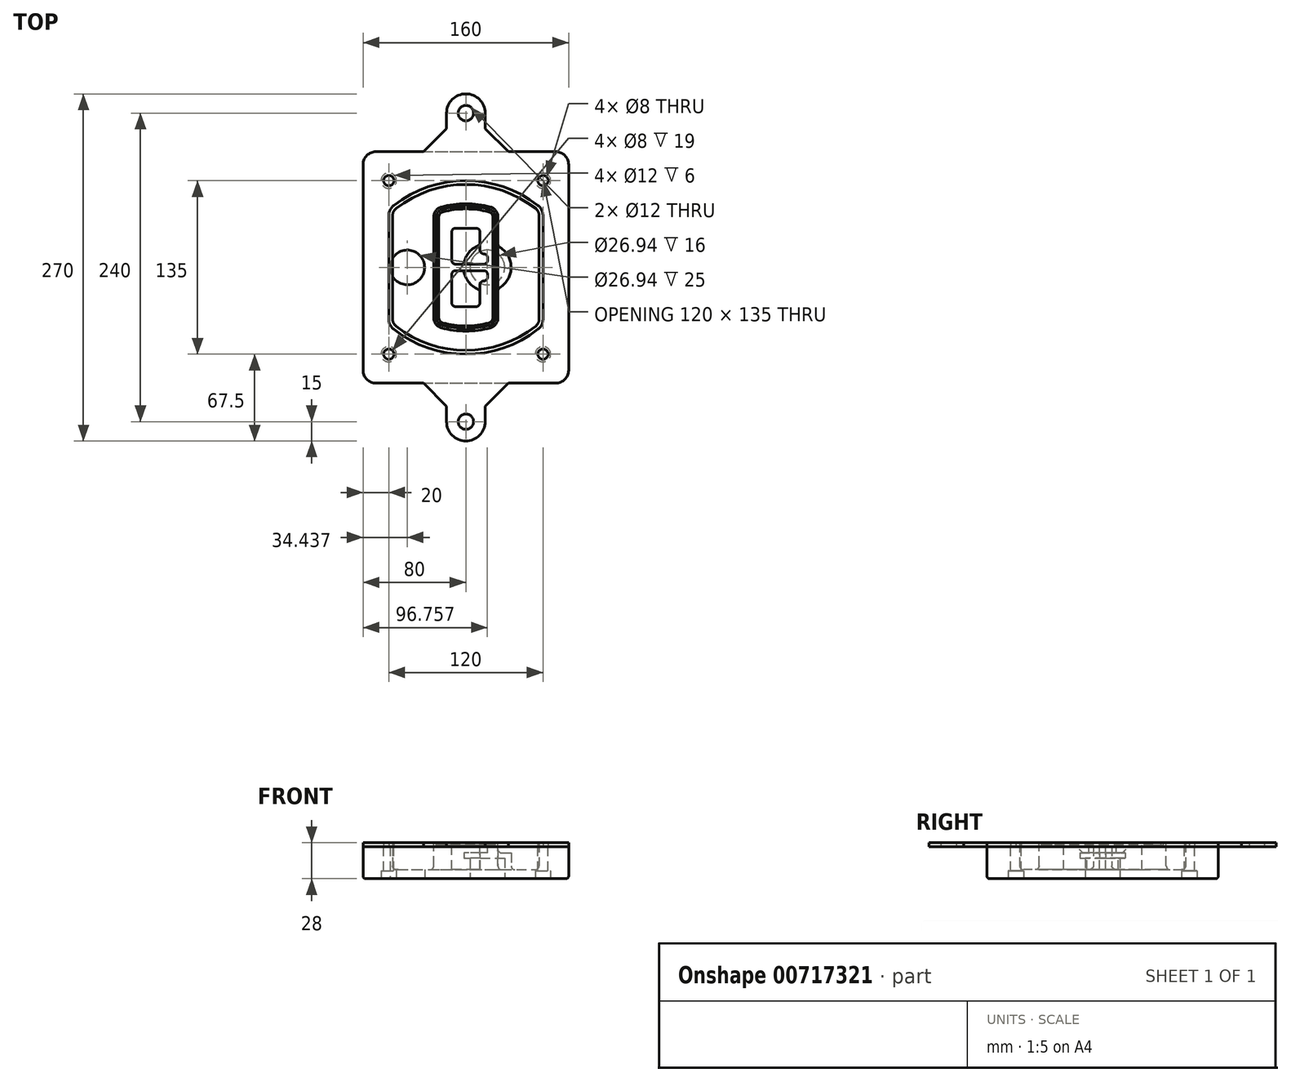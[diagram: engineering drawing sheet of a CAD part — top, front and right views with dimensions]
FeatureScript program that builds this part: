
annotation { "Feature Type Name" : "Feature", "Feature Type Description" : "" }
export const myFeature = defineFeature(function(context is Context, id is Id, definition is map)
    precondition{}
    {
        {
            var Q0;
            Q0=qCreatedBy(makeId("Top.planeOp"),FACE);
            var sketch = newSketch(context, id + "F0", { "sketchPlane" : qUnion([Q0])});
            skPoint(sketch, "E0.rect.middle", {"position": v(0, 0) * mm});
            skLineSegment(sketch, "E1.bottom", {"start": v(-70, -90) * mm, "end": v(70, -90) * mm});
            skLineSegment(sketch, "E1.top", {"start": v(-70, 90) * mm, "end": v(70, 90) * mm});
            skLineSegment(sketch, "E1.left", {"start": v(-80, -80) * mm, "end": v(-80, 80) * mm});
            skLineSegment(sketch, "E1.right", {"start": v(80, -80) * mm, "end": v(80, 80) * mm});
            skLineSegment(sketch, "E2", {"start": v(-80, 90) * mm, "end": v(80, -90) * mm, "construction": true});
            skLineSegment(sketch, "E3", {"start": v(80, 90) * mm, "end": v(-80, -90) * mm, "construction": true});
            skCircle(sketch, "E4", {"center": v(-60, 67.5) * mm, "radius": 4 * mm});
            skCircle(sketch, "E5", {"center": v(60, 67.5) * mm, "radius": 4 * mm});
            skCircle(sketch, "E6", {"center": v(60, -67.5) * mm, "radius": 4 * mm});
            skCircle(sketch, "E7", {"center": v(-60, -67.5) * mm, "radius": 4 * mm});
            skLineSegment(sketch, "E8", {"start": v(-60, 67.5) * mm, "end": v(60, 67.5) * mm, "construction": true});
            skLineSegment(sketch, "E9", {"start": v(60, 67.5) * mm, "end": v(60, -67.5) * mm, "construction": true});
            skLineSegment(sketch, "E10", {"start": v(60, -67.5) * mm, "end": v(-60, -67.5) * mm, "construction": true});
            skLineSegment(sketch, "E11", {"start": v(-60, -67.5) * mm, "end": v(-60, 67.5) * mm, "construction": true});
            skLineSegment(sketch, "E12", {"start": v(-60, 40.3) * mm, "end": v(-60, -40.3) * mm});
            skLineSegment(sketch, "E13", {"start": v(60, 40.3) * mm, "end": v(60, -40.3) * mm});
            skArc(sketch, "E14", {"start": v(56.15, 48.18) * mm, "mid": v(0, 67.5) * mm, "end": v(-56.15, 48.18) * mm});
            skArc(sketch, "E15", {"start": v(-56.15, -48.18) * mm, "mid": v(0, -67.5) * mm, "end": v(56.15, -48.18) * mm});
            skLineSegment(sketch, "E16", {"start": v(-60, 0) * mm, "end": v(60, 0) * mm, "construction": true});
            skPoint(sketch, "E17.visualSharp", {"position": v(-60, -45) * mm});
            skArc(sketch, "E17.filletArc", {"start": v(-60, -40.3) * mm, "mid": v(-58.99, -44.68) * mm, "end": v(-56.15, -48.18) * mm});
            skPoint(sketch, "E18.visualSharp", {"position": v(-60, 45) * mm});
            skArc(sketch, "E18.filletArc", {"start": v(-56.15, 48.18) * mm, "mid": v(-58.99, 44.68) * mm, "end": v(-60, 40.3) * mm});
            skPoint(sketch, "E19.visualSharp", {"position": v(60, 45) * mm});
            skArc(sketch, "E19.filletArc", {"start": v(60, 40.3) * mm, "mid": v(58.99, 44.68) * mm, "end": v(56.15, 48.18) * mm});
            skPoint(sketch, "E20.visualSharp", {"position": v(60, -45) * mm});
            skArc(sketch, "E20.filletArc", {"start": v(56.15, -48.18) * mm, "mid": v(58.99, -44.68) * mm, "end": v(60, -40.3) * mm});
            skPoint(sketch, "E21.visualSharp", {"position": v(-80, 90) * mm});
            skArc(sketch, "E21.filletArc", {"start": v(-70, 90) * mm, "mid": v(-77.07, 87.07) * mm, "end": v(-80, 80) * mm});
            skPoint(sketch, "E22.visualSharp", {"position": v(80, 90) * mm});
            skArc(sketch, "E22.filletArc", {"start": v(80, 80) * mm, "mid": v(77.07, 87.07) * mm, "end": v(70, 90) * mm});
            skPoint(sketch, "E23.visualSharp", {"position": v(80, -90) * mm});
            skArc(sketch, "E23.filletArc", {"start": v(70, -90) * mm, "mid": v(77.07, -87.07) * mm, "end": v(80, -80) * mm});
            skPoint(sketch, "E24.visualSharp", {"position": v(-80, -90) * mm});
            skArc(sketch, "E24.filletArc", {"start": v(-80, -80) * mm, "mid": v(-77.07, -87.07) * mm, "end": v(-70, -90) * mm});
            skArc(sketch, "E25.0", {"start": v(57, 40.3) * mm, "mid": v(56.3, 43.36) * mm, "end": v(54.3, 45.81) * mm});
            skLineSegment(sketch, "E25.1", {"start": v(57, 40.3) * mm, "end": v(57, -40.3) * mm});
            skArc(sketch, "E25.2", {"start": v(54.3, -45.81) * mm, "mid": v(56.3, -43.36) * mm, "end": v(57, -40.3) * mm});
            skArc(sketch, "E25.3", {"start": v(-54.3, -45.81) * mm, "mid": v(0, -64.5) * mm, "end": v(54.3, -45.81) * mm});
            skArc(sketch, "E25.4", {"start": v(-57, -40.3) * mm, "mid": v(-56.3, -43.36) * mm, "end": v(-54.3, -45.81) * mm});
            skArc(sketch, "E25.5", {"start": v(54.3, 45.81) * mm, "mid": v(0, 64.5) * mm, "end": v(-54.3, 45.81) * mm});
            skLineSegment(sketch, "E25.6", {"start": v(-57, 40.3) * mm, "end": v(-57, -40.3) * mm});
            skArc(sketch, "E25.7", {"start": v(-54.3, 45.81) * mm, "mid": v(-56.3, 43.36) * mm, "end": v(-57, 40.3) * mm});
            skArc(sketch, "E26.0", {"start": v(-58.62, 51.33) * mm, "mid": v(-62.58, 46.43) * mm, "end": v(-64, 40.3) * mm});
            skArc(sketch, "E26.1", {"start": v(58.62, 51.33) * mm, "mid": v(0, 71.5) * mm, "end": v(-58.62, 51.33) * mm});
            skArc(sketch, "E26.2", {"start": v(64, 40.3) * mm, "mid": v(62.58, 46.43) * mm, "end": v(58.62, 51.33) * mm});
            skLineSegment(sketch, "E26.3", {"start": v(64, 40.3) * mm, "end": v(64, -40.3) * mm});
            skArc(sketch, "E26.4", {"start": v(58.62, -51.33) * mm, "mid": v(62.58, -46.43) * mm, "end": v(64, -40.3) * mm});
            skLineSegment(sketch, "E26.5", {"start": v(-64, 40.3) * mm, "end": v(-64, -40.3) * mm});
            skArc(sketch, "E26.6", {"start": v(-58.62, -51.33) * mm, "mid": v(0, -71.5) * mm, "end": v(58.62, -51.33) * mm});
            skArc(sketch, "E26.7", {"start": v(-64, -40.3) * mm, "mid": v(-62.58, -46.43) * mm, "end": v(-58.62, -51.33) * mm});
            skSolve(sketch);
        }
        {
            var Q0;
            Q0=makeQuery(id+"F0.imprint","IMPRINT",FACE,{"disambiguationData":[TD([[makeQuery(id+"F0.imprint","IMPRINT",EDGE,{"derivedFrom":sQuery(id+"F0.wireOp",EDGE,"E1.bottom")}),1.0]])]});
            var Q1;
            Q1=makeQuery(id+"F0.imprint","IMPRINT",FACE,{"disambiguationData":[TD([[makeQuery(id+"F0.imprint","IMPRINT",EDGE,{"derivedFrom":sQuery(id+"F0.wireOp",EDGE,"E12")}),1.0]])]});
            var Q2;
            Q2=makeQuery(id+"F0.imprint","IMPRINT",FACE,{"disambiguationData":[TD([[makeQuery(id+"F0.imprint","IMPRINT",EDGE,{"derivedFrom":sQuery(id+"F0.wireOp",EDGE,"E25.0")}),1.0]])]});
            var Q3;
            Q3=makeQuery(id+"F0.imprint","IMPRINT",FACE,{"disambiguationData":[TD([[makeQuery(id+"F0.imprint","IMPRINT",EDGE,{"derivedFrom":sQuery(id+"F0.wireOp",EDGE,"E12")}),-1.0]])]});
            extrude(context, id + "F1", {"entities" : qUnion([Q0, Q1, Q2, Q3]), "oppositeDirection" : true, "depth" : 25 * mm});
        }
        {
            var Q0;
            Q0=makeQuery(id+"F0.imprint","IMPRINT",FACE,{"disambiguationData":[TD([[makeQuery(id+"F0.imprint","IMPRINT",EDGE,{"derivedFrom":sQuery(id+"F0.wireOp",EDGE,"E12")}),1.0]])]});
            extrude(context, id + "F2", {"entities" : qUnion([Q0]), "operationType" : NewBodyOperationType.ADD, "depth" : 3 * mm});
        }
        {
            var Q0;
            Q0=makeQuery(id+"F0.imprint","IMPRINT",FACE,{"disambiguationData":[TD([[makeQuery(id+"F0.imprint","IMPRINT",EDGE,{"derivedFrom":sQuery(id+"F0.wireOp",EDGE,"E25.0")}),1.0]])]});
            extrude(context, id + "F3", {"entities" : qUnion([Q0]), "operationType" : NewBodyOperationType.REMOVE, "oppositeDirection" : true, "depth" : 18 * mm});
        }
        {
            var Q0;
            Q0=makeQuery(id+"F2.opExtrude","CAP_FACE",FACE,{"disambiguationData":[OSD([sQuery(id+"F0.wireOp",EDGE,"E12"),sQuery(id+"F0.wireOp",EDGE,"E13"),sQuery(id+"F0.wireOp",EDGE,"E14"),sQuery(id+"F0.wireOp",EDGE,"E15"),sQuery(id+"F0.wireOp",EDGE,"E17.filletArc"),sQuery(id+"F0.wireOp",EDGE,"E18.filletArc"),sQuery(id+"F0.wireOp",EDGE,"E19.filletArc"),sQuery(id+"F0.wireOp",EDGE,"E20.filletArc"),sQuery(id+"F0.wireOp",EDGE,"E25.0"),sQuery(id+"F0.wireOp",EDGE,"E25.1"),sQuery(id+"F0.wireOp",EDGE,"E25.2"),sQuery(id+"F0.wireOp",EDGE,"E25.3"),sQuery(id+"F0.wireOp",EDGE,"E25.4"),sQuery(id+"F0.wireOp",EDGE,"E25.5"),sQuery(id+"F0.wireOp",EDGE,"E25.6"),sQuery(id+"F0.wireOp",EDGE,"E25.7")])],"isStart":false});
            var sketch = newSketch(context, id + "F4", { "sketchPlane" : qUnion([Q0])});
            skArc(sketch, "E27.0", {"start": v(-19.08, -46.97) * mm, "mid": v(0, -49.5) * mm, "end": v(19.08, -46.97) * mm});
            skArc(sketch, "E28.0", {"start": v(19.08, 46.97) * mm, "mid": v(0, 49.5) * mm, "end": v(-19.08, 46.97) * mm});
            skLineSegment(sketch, "E29", {"start": v(-25, 39.25) * mm, "end": v(-25, -39.25) * mm});
            skLineSegment(sketch, "E30", {"start": v(25, 39.25) * mm, "end": v(25, -39.25) * mm});
            skLineSegment(sketch, "E31", {"start": v(-25, 45.1) * mm, "end": v(25, 45.1) * mm, "construction": true});
            skLineSegment(sketch, "E32", {"start": v(-25, -45.1) * mm, "end": v(25, -45.1) * mm, "construction": true});
            skPoint(sketch, "E33.visualSharp", {"position": v(-25, 45.1) * mm});
            skArc(sketch, "E33.filletArc", {"start": v(-19.08, 46.97) * mm, "mid": v(-23.35, 44.11) * mm, "end": v(-25, 39.25) * mm});
            skPoint(sketch, "E34.visualSharp", {"position": v(25, 45.1) * mm});
            skArc(sketch, "E34.filletArc", {"start": v(25, 39.25) * mm, "mid": v(23.35, 44.11) * mm, "end": v(19.08, 46.97) * mm});
            skPoint(sketch, "E35.visualSharp", {"position": v(25, -45.1) * mm});
            skArc(sketch, "E35.filletArc", {"start": v(19.08, -46.97) * mm, "mid": v(23.35, -44.11) * mm, "end": v(25, -39.25) * mm});
            skPoint(sketch, "E36.visualSharp", {"position": v(-25, -45.1) * mm});
            skArc(sketch, "E36.filletArc", {"start": v(-25, -39.25) * mm, "mid": v(-23.35, -44.11) * mm, "end": v(-19.08, -46.97) * mm});
            skArc(sketch, "E37.0", {"start": v(54.3, 45.81) * mm, "mid": v(0, 64.5) * mm, "end": v(-54.3, 45.81) * mm});
            skArc(sketch, "E37.1", {"start": v(-54.3, 45.81) * mm, "mid": v(-56.3, 43.36) * mm, "end": v(-57, 40.3) * mm});
            skLineSegment(sketch, "E37.2", {"start": v(-57, 40.3) * mm, "end": v(-57, -40.3) * mm});
            skArc(sketch, "E37.3", {"start": v(-57, -40.3) * mm, "mid": v(-56.3, -43.36) * mm, "end": v(-54.3, -45.81) * mm});
            skArc(sketch, "E37.4", {"start": v(-54.3, -45.81) * mm, "mid": v(0, -64.5) * mm, "end": v(54.3, -45.81) * mm});
            skArc(sketch, "E37.5", {"start": v(54.3, -45.81) * mm, "mid": v(56.3, -43.36) * mm, "end": v(57, -40.3) * mm});
            skLineSegment(sketch, "E37.6", {"start": v(57, 40.3) * mm, "end": v(57, -40.3) * mm});
            skArc(sketch, "E37.7", {"start": v(57, 40.3) * mm, "mid": v(56.3, 43.36) * mm, "end": v(54.3, 45.81) * mm});
            skLineSegment(sketch, "E38.0", {"start": v(23, 39.25) * mm, "end": v(23, -39.25) * mm});
            skArc(sketch, "E38.1", {"start": v(18.56, -45.04) * mm, "mid": v(21.76, -42.9) * mm, "end": v(23, -39.25) * mm});
            skArc(sketch, "E38.2", {"start": v(-18.56, -45.04) * mm, "mid": v(0, -47.5) * mm, "end": v(18.56, -45.04) * mm});
            skArc(sketch, "E38.3", {"start": v(-23, -39.25) * mm, "mid": v(-21.76, -42.9) * mm, "end": v(-18.56, -45.04) * mm});
            skLineSegment(sketch, "E38.4", {"start": v(-23, 39.25) * mm, "end": v(-23, -39.25) * mm});
            skArc(sketch, "E38.5", {"start": v(23, 39.25) * mm, "mid": v(21.76, 42.9) * mm, "end": v(18.56, 45.04) * mm});
            skArc(sketch, "E38.6", {"start": v(-18.56, 45.04) * mm, "mid": v(-21.76, 42.9) * mm, "end": v(-23, 39.25) * mm});
            skArc(sketch, "E38.7", {"start": v(18.56, 45.04) * mm, "mid": v(0, 47.5) * mm, "end": v(-18.56, 45.04) * mm});
            skArc(sketch, "E39.0", {"start": v(21, 39.25) * mm, "mid": v(20.18, 41.68) * mm, "end": v(18.04, 43.1) * mm});
            skLineSegment(sketch, "E39.1", {"start": v(21, 39.25) * mm, "end": v(21, -39.25) * mm});
            skArc(sketch, "E39.2", {"start": v(18.04, -43.1) * mm, "mid": v(20.18, -41.68) * mm, "end": v(21, -39.25) * mm});
            skArc(sketch, "E39.3", {"start": v(-18.04, -43.1) * mm, "mid": v(0, -45.5) * mm, "end": v(18.04, -43.1) * mm});
            skArc(sketch, "E39.4", {"start": v(-21, -39.25) * mm, "mid": v(-20.18, -41.68) * mm, "end": v(-18.04, -43.1) * mm});
            skArc(sketch, "E39.5", {"start": v(18.04, 43.1) * mm, "mid": v(0, 45.5) * mm, "end": v(-18.04, 43.1) * mm});
            skLineSegment(sketch, "E39.6", {"start": v(-21, 39.25) * mm, "end": v(-21, -39.25) * mm});
            skArc(sketch, "E39.7", {"start": v(-18.04, 43.1) * mm, "mid": v(-20.18, 41.68) * mm, "end": v(-21, 39.25) * mm});
            skLineSegment(sketch, "E40", {"start": v(-25, 0) * mm, "end": v(25, 0) * mm, "construction": true});
            skLineSegment(sketch, "E41", {"start": v(-11, 5.5) * mm, "end": v(-11, 27.5) * mm});
            skLineSegment(sketch, "E42", {"start": v(-8, 30.5) * mm, "end": v(8, 30.5) * mm});
            skLineSegment(sketch, "E43", {"start": v(11, 27.5) * mm, "end": v(11, 13.5) * mm});
            skLineSegment(sketch, "E44", {"start": v(14, 10.5) * mm, "end": v(14, 10.5) * mm});
            skLineSegment(sketch, "E45", {"start": v(17, 7.5) * mm, "end": v(17, 5.5) * mm});
            skLineSegment(sketch, "E46", {"start": v(14, 2.5) * mm, "end": v(-8, 2.5) * mm});
            skPoint(sketch, "E47.visualSharp", {"position": v(-11, 30.5) * mm});
            skArc(sketch, "E47.filletArc", {"start": v(-8, 30.5) * mm, "mid": v(-10.12, 29.62) * mm, "end": v(-11, 27.5) * mm});
            skPoint(sketch, "E48.visualSharp", {"position": v(11, 30.5) * mm});
            skArc(sketch, "E48.filletArc", {"start": v(11, 27.5) * mm, "mid": v(10.12, 29.62) * mm, "end": v(8, 30.5) * mm});
            skPoint(sketch, "E49.visualSharp", {"position": v(11, 10.5) * mm});
            skArc(sketch, "E49.filletArc", {"start": v(11, 13.5) * mm, "mid": v(11.88, 11.38) * mm, "end": v(14, 10.5) * mm});
            skPoint(sketch, "E50.visualSharp", {"position": v(17, 10.5) * mm});
            skArc(sketch, "E50.filletArc", {"start": v(17, 7.5) * mm, "mid": v(16.12, 9.62) * mm, "end": v(14, 10.5) * mm});
            skPoint(sketch, "E51.visualSharp", {"position": v(17, 2.5) * mm});
            skArc(sketch, "E51.filletArc", {"start": v(14, 2.5) * mm, "mid": v(16.12, 3.38) * mm, "end": v(17, 5.5) * mm});
            skPoint(sketch, "E52.visualSharp", {"position": v(-11, 2.5) * mm});
            skArc(sketch, "E52.filletArc", {"start": v(-11, 5.5) * mm, "mid": v(-10.12, 3.38) * mm, "end": v(-8, 2.5) * mm});
            skLineSegment(sketch, "E53.0.MirrorCS", {"start": v(14, -2.5) * mm, "end": v(-8, -2.5) * mm});
            skArc(sketch, "E54.0.MirrorCS", {"start": v(-11, -5.5) * mm, "mid": v(-10.12, -3.38) * mm, "end": v(-8, -2.5) * mm});
            skLineSegment(sketch, "E55.0.MirrorCS", {"start": v(-11, -5.5) * mm, "end": v(-11, -27.5) * mm});
            skArc(sketch, "E56.0.MirrorCS", {"start": v(-8, -30.5) * mm, "mid": v(-10.12, -29.62) * mm, "end": v(-11, -27.5) * mm});
            skLineSegment(sketch, "E57.0.MirrorCS", {"start": v(-8, -30.5) * mm, "end": v(8, -30.5) * mm});
            skArc(sketch, "E58.0.MirrorCS", {"start": v(11, -27.5) * mm, "mid": v(10.12, -29.62) * mm, "end": v(8, -30.5) * mm});
            skLineSegment(sketch, "E59.0.MirrorCS", {"start": v(11, -27.5) * mm, "end": v(11, -13.5) * mm});
            skArc(sketch, "E60.0.MirrorCS", {"start": v(11, -13.5) * mm, "mid": v(11.88, -11.38) * mm, "end": v(14, -10.5) * mm});
            skArc(sketch, "E61.0.MirrorCS", {"start": v(17, -7.5) * mm, "mid": v(16.12, -9.62) * mm, "end": v(14, -10.5) * mm});
            skLineSegment(sketch, "E62.0.MirrorCS", {"start": v(17, -7.5) * mm, "end": v(17, -5.5) * mm});
            skArc(sketch, "E63.0.MirrorCS", {"start": v(14, -2.5) * mm, "mid": v(16.12, -3.38) * mm, "end": v(17, -5.5) * mm});
            skSolve(sketch);
        }
        {
            var Q0;
            Q0=makeQuery(id+"F4.imprint","IMPRINT",FACE,{"disambiguationData":[TD([[makeQuery(id+"F4.imprint","IMPRINT",EDGE,{"derivedFrom":sQuery(id+"F4.wireOp",EDGE,"E27.0")}),1.0]])]});
            var Q1;
            Q1=makeQuery(id+"F4.imprint","IMPRINT",FACE,{"disambiguationData":[TD([[makeQuery(id+"F4.imprint","IMPRINT",EDGE,{"derivedFrom":sQuery(id+"F4.wireOp",EDGE,"E38.0")}),-1.0]])]});
            var Q2;
            Q2=makeQuery(id+"F4.imprint","IMPRINT",FACE,{"disambiguationData":[TD([[makeQuery(id+"F4.imprint","IMPRINT",EDGE,{"derivedFrom":sQuery(id+"F4.wireOp",EDGE,"E39.0")}),1.0]])]});
            extrude(context, id + "F5", {"entities" : qUnion([Q0, Q1, Q2]), "operationType" : NewBodyOperationType.ADD, "endBound" : BoundingType.UP_TO_NEXT, "oppositeDirection" : true, "depth" : 25 * mm});
        }
        {
            var Q0;
            Q0=makeQuery(id+"F4.imprint","IMPRINT",FACE,{"disambiguationData":[TD([[makeQuery(id+"F4.imprint","IMPRINT",EDGE,{"derivedFrom":sQuery(id+"F4.wireOp",EDGE,"E38.0")}),-1.0]])]});
            extrude(context, id + "F6", {"entities" : qUnion([Q0]), "operationType" : NewBodyOperationType.REMOVE, "oppositeDirection" : true, "depth" : 2 * mm});
        }
        {
            var Q0;
            Q0=makeQuery(id+"F1.opExtrude","CAP_FACE",FACE,{"disambiguationData":[OSD([sQuery(id+"F0.wireOp",EDGE,"E1.bottom"),sQuery(id+"F0.wireOp",EDGE,"E1.top"),sQuery(id+"F0.wireOp",EDGE,"E1.left"),sQuery(id+"F0.wireOp",EDGE,"E1.right"),sQuery(id+"F0.wireOp",EDGE,"E4"),sQuery(id+"F0.wireOp",EDGE,"E5"),sQuery(id+"F0.wireOp",EDGE,"E6"),sQuery(id+"F0.wireOp",EDGE,"E7"),sQuery(id+"F0.wireOp",EDGE,"E21.filletArc"),sQuery(id+"F0.wireOp",EDGE,"E22.filletArc"),sQuery(id+"F0.wireOp",EDGE,"E23.filletArc"),sQuery(id+"F0.wireOp",EDGE,"E24.filletArc")])],"isStart":false});
            var sketch = newSketch(context, id + "F7", { "sketchPlane" : qUnion([Q0])});
            skCircle(sketch, "E64", {"center": v(16.76, 0) * mm, "radius": 13.47 * mm});
            skCircle(sketch, "E65", {"center": v(-45.56, 0) * mm, "radius": 13.47 * mm});
            skLineSegment(sketch, "E66", {"start": v(80, 0) * mm, "end": v(-80, 0) * mm});
            skCircle(sketch, "E67", {"center": v(16.76, 0) * mm, "radius": 18.47 * mm});
            skCircle(sketch, "E68", {"center": v(60, -67.5) * mm, "radius": 6 * mm});
            skCircle(sketch, "E69", {"center": v(-60, -67.5) * mm, "radius": 6 * mm});
            skCircle(sketch, "E70", {"center": v(-60, 67.5) * mm, "radius": 6 * mm});
            skCircle(sketch, "E71", {"center": v(60, 67.5) * mm, "radius": 6 * mm});
            skSolve(sketch);
        }
        {
            var Q0;
            {var subQ1=sQuery(id+"F7.wireOp",EDGE,"E66");var subQ4=sQuery(id+"F7.wireOp",EDGE,"E64");var subQ6=makeQuery(id+"F7.imprint","INTERSECT",VERTEX,{"disambiguationData":[OD(0.0)],"derivedFrom":[subQ4,subQ1]});Q0=makeQuery(id+"F7.imprint","IMPRINT",FACE,{"disambiguationData":[TD([[makeQuery(id+"F7.imprint","IMPRINT",EDGE,{"disambiguationData":[TD([[subQ6,-1.0]])],"derivedFrom":subQ4}),-1.0]])]});}
            var Q1;
            {var subQ0=sQuery(id+"F7.wireOp",EDGE,"E66");var subQ1=sQuery(id+"F7.wireOp",EDGE,"E64");var subQ3=makeQuery(id+"F7.imprint","INTERSECT",VERTEX,{"disambiguationData":[OD(0.0)],"derivedFrom":[subQ1,subQ0]});Q1=makeQuery(id+"F7.imprint","IMPRINT",FACE,{"disambiguationData":[TD([[makeQuery(id+"F7.imprint","IMPRINT",EDGE,{"disambiguationData":[TD([[subQ3,-1.0]])],"derivedFrom":subQ1}),1.0]])]});}
            var Q2;
            {var subQ0=sQuery(id+"F7.wireOp",EDGE,"E66");var subQ1=sQuery(id+"F7.wireOp",EDGE,"E64");var subQ3=makeQuery(id+"F7.imprint","INTERSECT",VERTEX,{"disambiguationData":[OD(0.0)],"derivedFrom":[subQ1,subQ0]});Q2=makeQuery(id+"F7.imprint","IMPRINT",FACE,{"disambiguationData":[TD([[makeQuery(id+"F7.imprint","IMPRINT",EDGE,{"disambiguationData":[TD([[subQ3,1.0]])],"derivedFrom":subQ1}),1.0]])]});}
            var Q3;
            {var subQ1=sQuery(id+"F7.wireOp",EDGE,"E66");var subQ4=sQuery(id+"F7.wireOp",EDGE,"E64");var subQ6=makeQuery(id+"F7.imprint","INTERSECT",VERTEX,{"disambiguationData":[OD(0.0)],"derivedFrom":[subQ4,subQ1]});Q3=makeQuery(id+"F7.imprint","IMPRINT",FACE,{"disambiguationData":[TD([[makeQuery(id+"F7.imprint","IMPRINT",EDGE,{"disambiguationData":[TD([[subQ6,1.0]])],"derivedFrom":subQ4}),-1.0]])]});}
            extrude(context, id + "F8", {"entities" : qUnion([Q0, Q1, Q2, Q3]), "operationType" : NewBodyOperationType.ADD, "oppositeDirection" : true, "depth" : 20 * mm});
        }
        {
            var Q0;
            {var subQ0=sQuery(id+"F7.wireOp",EDGE,"E66");var subQ1=sQuery(id+"F7.wireOp",EDGE,"E64");var subQ3=makeQuery(id+"F7.imprint","INTERSECT",VERTEX,{"disambiguationData":[OD(0.0)],"derivedFrom":[subQ1,subQ0]});Q0=makeQuery(id+"F7.imprint","IMPRINT",FACE,{"disambiguationData":[TD([[makeQuery(id+"F7.imprint","IMPRINT",EDGE,{"disambiguationData":[TD([[subQ3,-1.0]])],"derivedFrom":subQ1}),1.0]])]});}
            var Q1;
            {var subQ0=sQuery(id+"F7.wireOp",EDGE,"E66");var subQ1=sQuery(id+"F7.wireOp",EDGE,"E64");var subQ3=makeQuery(id+"F7.imprint","INTERSECT",VERTEX,{"disambiguationData":[OD(0.0)],"derivedFrom":[subQ1,subQ0]});Q1=makeQuery(id+"F7.imprint","IMPRINT",FACE,{"disambiguationData":[TD([[makeQuery(id+"F7.imprint","IMPRINT",EDGE,{"disambiguationData":[TD([[subQ3,1.0]])],"derivedFrom":subQ1}),1.0]])]});}
            extrude(context, id + "F9", {"entities" : qUnion([Q0, Q1]), "operationType" : NewBodyOperationType.REMOVE, "oppositeDirection" : true, "depth" : 16 * mm});
        }
        {
            var Q0;
            {var subQ0=sQuery(id+"F7.wireOp",EDGE,"E66");var subQ1=sQuery(id+"F7.wireOp",EDGE,"E65");var subQ3=makeQuery(id+"F7.imprint","INTERSECT",VERTEX,{"disambiguationData":[OD(0.0)],"derivedFrom":[subQ1,subQ0]});Q0=makeQuery(id+"F7.imprint","IMPRINT",FACE,{"disambiguationData":[TD([[makeQuery(id+"F7.imprint","IMPRINT",EDGE,{"disambiguationData":[TD([[subQ3,-1.0]])],"derivedFrom":subQ1}),1.0]])]});}
            var Q1;
            {var subQ0=sQuery(id+"F7.wireOp",EDGE,"E66");var subQ1=sQuery(id+"F7.wireOp",EDGE,"E65");var subQ3=makeQuery(id+"F7.imprint","INTERSECT",VERTEX,{"disambiguationData":[OD(0.0)],"derivedFrom":[subQ1,subQ0]});Q1=makeQuery(id+"F7.imprint","IMPRINT",FACE,{"disambiguationData":[TD([[makeQuery(id+"F7.imprint","IMPRINT",EDGE,{"disambiguationData":[TD([[subQ3,1.0]])],"derivedFrom":subQ1}),1.0]])]});}
            extrude(context, id + "F10", {"entities" : qUnion([Q0, Q1]), "operationType" : NewBodyOperationType.REMOVE, "oppositeDirection" : true, "depth" : 25 * mm});
        }
        {
            var Q0;
            Q0=makeQuery(id+"F7.imprint","IMPRINT",FACE,{"disambiguationData":[TD([[makeQuery(id+"F7.imprint","IMPRINT",EDGE,{"derivedFrom":sQuery(id+"F7.wireOp",EDGE,"E68")}),1.0]])]});
            var Q1;
            Q1=makeQuery(id+"F7.imprint","IMPRINT",FACE,{"disambiguationData":[TD([[makeQuery(id+"F7.imprint","IMPRINT",EDGE,{"derivedFrom":makeQuery(id+"F1.opExtrude","CAP_EDGE",EDGE,{"disambiguationData":[OSD([sQuery(id+"F0.wireOp",EDGE,"E5")])],"isStart":false})}),-1.0]])]});
            var Q2;
            Q2=makeQuery(id+"F7.imprint","IMPRINT",FACE,{"disambiguationData":[TD([[makeQuery(id+"F7.imprint","IMPRINT",EDGE,{"derivedFrom":sQuery(id+"F7.wireOp",EDGE,"E69")}),1.0]])]});
            var Q3;
            Q3=makeQuery(id+"F7.imprint","IMPRINT",FACE,{"disambiguationData":[TD([[makeQuery(id+"F7.imprint","IMPRINT",EDGE,{"derivedFrom":makeQuery(id+"F1.opExtrude","CAP_EDGE",EDGE,{"disambiguationData":[OSD([sQuery(id+"F0.wireOp",EDGE,"E4")])],"isStart":false})}),-1.0]])]});
            var Q4;
            Q4=makeQuery(id+"F7.imprint","IMPRINT",FACE,{"disambiguationData":[TD([[makeQuery(id+"F7.imprint","IMPRINT",EDGE,{"derivedFrom":sQuery(id+"F7.wireOp",EDGE,"E70")}),1.0]])]});
            var Q5;
            Q5=makeQuery(id+"F7.imprint","IMPRINT",FACE,{"disambiguationData":[TD([[makeQuery(id+"F7.imprint","IMPRINT",EDGE,{"derivedFrom":makeQuery(id+"F1.opExtrude","CAP_EDGE",EDGE,{"disambiguationData":[OSD([sQuery(id+"F0.wireOp",EDGE,"E7")])],"isStart":false})}),-1.0]])]});
            var Q6;
            Q6=makeQuery(id+"F7.imprint","IMPRINT",FACE,{"disambiguationData":[TD([[makeQuery(id+"F7.imprint","IMPRINT",EDGE,{"derivedFrom":sQuery(id+"F7.wireOp",EDGE,"E71")}),1.0]])]});
            var Q7;
            Q7=makeQuery(id+"F7.imprint","IMPRINT",FACE,{"disambiguationData":[TD([[makeQuery(id+"F7.imprint","IMPRINT",EDGE,{"derivedFrom":makeQuery(id+"F1.opExtrude","CAP_EDGE",EDGE,{"disambiguationData":[OSD([sQuery(id+"F0.wireOp",EDGE,"E6")])],"isStart":false})}),-1.0]])]});
            extrude(context, id + "F11", {"entities" : qUnion([Q0, Q1, Q2, Q3, Q4, Q5, Q6, Q7]), "operationType" : NewBodyOperationType.REMOVE, "oppositeDirection" : true, "depth" : 6 * mm});
        }
        {
            var Q0;
            Q0=makeQuery(id+"F9.boolean.opBoolean","COPY",FACE,{"derivedFrom":makeQuery(id+"F9.opExtrude","CAP_FACE",FACE,{"disambiguationData":[OSD([sQuery(id+"F7.wireOp",EDGE,"E64")])],"isStart":false})});
            var sketch = newSketch(context, id + "F12", { "sketchPlane" : qUnion([Q0])});
            skArc(sketch, "E72.0", {"start": v(11, 17.55) * mm, "mid": v(2.57, 11.82) * mm, "end": v(-1.54, 2.5) * mm});
            skArc(sketch, "E72.1", {"start": v(-1.54, -2.5) * mm, "mid": v(2.57, -11.82) * mm, "end": v(11, -17.55) * mm});
            skLineSegment(sketch, "E73", {"start": v(-1.54, -2.5) * mm, "end": v(14, -2.5) * mm});
            skLineSegment(sketch, "E74.0", {"start": v(14, 2.5) * mm, "end": v(-1.54, 2.5) * mm});
            skArc(sketch, "E74.1", {"start": v(14, 2.5) * mm, "mid": v(16.12, 3.38) * mm, "end": v(17, 5.5) * mm});
            skLineSegment(sketch, "E74.2", {"start": v(17, 7.5) * mm, "end": v(17, 5.5) * mm});
            skArc(sketch, "E74.3", {"start": v(17, 7.5) * mm, "mid": v(16.12, 9.62) * mm, "end": v(14, 10.5) * mm});
            skArc(sketch, "E74.4", {"start": v(11, 13.5) * mm, "mid": v(11.88, 11.38) * mm, "end": v(14, 10.5) * mm});
            skLineSegment(sketch, "E74.5", {"start": v(11, 17.55) * mm, "end": v(11, 13.5) * mm});
            skLineSegment(sketch, "E74.7", {"start": v(14, -2.5) * mm, "end": v(-1.54, -2.5) * mm});
            skArc(sketch, "E74.8", {"start": v(14, -2.5) * mm, "mid": v(16.12, -3.38) * mm, "end": v(17, -5.5) * mm});
            skLineSegment(sketch, "E74.9", {"start": v(17, -7.5) * mm, "end": v(17, -5.5) * mm});
            skArc(sketch, "E74.10", {"start": v(17, -7.5) * mm, "mid": v(16.12, -9.62) * mm, "end": v(14, -10.5) * mm});
            skArc(sketch, "E74.11", {"start": v(11, -13.5) * mm, "mid": v(11.88, -11.38) * mm, "end": v(14, -10.5) * mm});
            skLineSegment(sketch, "E74.12", {"start": v(11, -17.55) * mm, "end": v(11, -13.5) * mm});
            skPoint(sketch, "E75.orphan", {"position": v(11, -27.5) * mm});
            skPoint(sketch, "E76.orphan", {"position": v(-8, -2.5) * mm});
            skPoint(sketch, "E77.orphan", {"position": v(-8, 2.5) * mm});
            skPoint(sketch, "E78.orphan", {"position": v(11, 27.5) * mm});
            skSolve(sketch);
        }
        {
            var Q0;
            {var subQ7=sQuery(id+"F12.wireOp",EDGE,"E72.0");var subQ14=sQuery(id+"F12.wireOp",EDGE,"E72.1");var subQ16=sQuery(id+"F12.wireOp",EDGE,"E74.1");var subQ18=sQuery(id+"F12.wireOp",EDGE,"E74.8");Q0=qUnion([makeQuery(id+"F12.imprint","IMPRINT",FACE,{"disambiguationData":[TD([[makeQuery(id+"F12.imprint","IMPRINT",EDGE,{"derivedFrom":subQ7}),1.0]])]}),makeQuery(id+"F12.imprint","IMPRINT",FACE,{"disambiguationData":[TD([[makeQuery(id+"F12.imprint","IMPRINT",EDGE,{"derivedFrom":subQ14}),1.0]])]}),makeQuery(id+"F12.imprint","IMPRINT",FACE,{"disambiguationData":[TD([[makeQuery(id+"F12.imprint","IMPRINT",EDGE,{"derivedFrom":subQ16}),1.0]])]}),makeQuery(id+"F12.imprint","IMPRINT",FACE,{"disambiguationData":[TD([[makeQuery(id+"F12.imprint","IMPRINT",EDGE,{"derivedFrom":subQ18}),-1.0]])]})]);}
            var Q1;
            Q1=makeQuery(id+"F5.boolean.opBoolean","SPLIT",FACE,{"disambiguationData":[TD([makeQuery(id+"F5.opExtrude","SWEPT_FACE",FACE,{"disambiguationData":[OSD([sQuery(id+"F4.wireOp",EDGE,"E41")])]})])],"derivedFrom":makeQuery(id+"F3.boolean.opBoolean","COPY",FACE,{"derivedFrom":makeQuery(id+"F3.opExtrude","CAP_FACE",FACE,{"disambiguationData":[OSD([sQuery(id+"F0.wireOp",EDGE,"E25.0"),sQuery(id+"F0.wireOp",EDGE,"E25.1"),sQuery(id+"F0.wireOp",EDGE,"E25.2"),sQuery(id+"F0.wireOp",EDGE,"E25.3"),sQuery(id+"F0.wireOp",EDGE,"E25.4"),sQuery(id+"F0.wireOp",EDGE,"E25.5"),sQuery(id+"F0.wireOp",EDGE,"E25.6"),sQuery(id+"F0.wireOp",EDGE,"E25.7")])],"isStart":false})})});
            extrude(context, id + "F13", {"entities" : qUnion([Q0]), "operationType" : NewBodyOperationType.REMOVE, "endBound" : BoundingType.UP_TO_SURFACE, "endBoundEntityFace" : qUnion([Q1]), "depth" : 25 * mm});
        }
        {
            var Q0;
            Q0=makeQuery(id+"F3.boolean.opBoolean","COPY",EDGE,{"derivedFrom":makeQuery(id+"F3.opExtrude","CAP_EDGE",EDGE,{"disambiguationData":[OSD([sQuery(id+"F0.wireOp",EDGE,"E25.6")])],"isStart":false})});
            var Q1;
            Q1=makeQuery(id+"F8.boolean.opBoolean","INTERSECT",EDGE,{"derivedFrom":[makeQuery(id+"F5.opExtrude","SWEPT_FACE",FACE,{"disambiguationData":[OSD([sQuery(id+"F4.wireOp",EDGE,"E30")])]}),makeQuery(id+"F8.opExtrude","CAP_FACE",FACE,{"disambiguationData":[OSD([sQuery(id+"F7.wireOp",EDGE,"E67")])],"isStart":false})]});
            var Q2;
            Q2=makeQuery(id+"F8.boolean.opBoolean","INTERSECT",EDGE,{"disambiguationData":[OD(1.0)],"derivedFrom":[makeQuery(id+"F5.opExtrude","SWEPT_FACE",FACE,{"disambiguationData":[OSD([sQuery(id+"F4.wireOp",EDGE,"E30")])]}),makeQuery(id+"F8.opExtrude","SWEPT_FACE",FACE,{"disambiguationData":[OSD([sQuery(id+"F7.wireOp",EDGE,"E67")])]})]});
            var Q3;
            {var subQ0=sQuery(id+"F4.wireOp",EDGE,"E30");Q3=makeQuery(id+"F8.boolean.opBoolean","SPLIT",EDGE,{"disambiguationData":[TD([makeQuery(id+"F5.opExtrude","SWEPT_FACE",FACE,{"disambiguationData":[OSD([sQuery(id+"F4.wireOp",EDGE,"E35.filletArc")])]})])],"derivedFrom":makeQuery(id+"F5.opExtrude","CAP_EDGE",EDGE,{"disambiguationData":[OSD([subQ0])],"isStart":false})});}
            var Q4;
            {var subQ0=sQuery(id+"F0.wireOp",EDGE,"E25.7");var subQ1=sQuery(id+"F0.wireOp",EDGE,"E25.1");var subQ2=sQuery(id+"F0.wireOp",EDGE,"E25.6");var subQ3=sQuery(id+"F0.wireOp",EDGE,"E25.5");var subQ4=sQuery(id+"F0.wireOp",EDGE,"E25.4");var subQ5=sQuery(id+"F0.wireOp",EDGE,"E25.0");var subQ6=sQuery(id+"F0.wireOp",EDGE,"E25.2");var subQ7=sQuery(id+"F0.wireOp",EDGE,"E25.3");Q4=makeQuery(id+"F8.boolean.opBoolean","INTERSECT",EDGE,{"derivedFrom":[makeQuery(id+"F5.boolean.opBoolean","SPLIT",FACE,{"disambiguationData":[TD([makeQuery(id+"F2.opExtrude","SWEPT_FACE",FACE,{"disambiguationData":[OSD([subQ5])]})])],"derivedFrom":makeQuery(id+"F3.boolean.opBoolean","COPY",FACE,{"derivedFrom":makeQuery(id+"F3.opExtrude","CAP_FACE",FACE,{"disambiguationData":[OSD([subQ5,subQ1,subQ6,subQ7,subQ4,subQ3,subQ2,subQ0])],"isStart":false})})}),makeQuery(id+"F8.opExtrude","SWEPT_FACE",FACE,{"disambiguationData":[OSD([sQuery(id+"F7.wireOp",EDGE,"E67")])]})]});}
            var Q5;
            Q5=makeQuery(id+"F8.boolean.opBoolean","INTERSECT",EDGE,{"disambiguationData":[OD(0.0)],"derivedFrom":[makeQuery(id+"F5.opExtrude","SWEPT_FACE",FACE,{"disambiguationData":[OSD([sQuery(id+"F4.wireOp",EDGE,"E30")])]}),makeQuery(id+"F8.opExtrude","SWEPT_FACE",FACE,{"disambiguationData":[OSD([sQuery(id+"F7.wireOp",EDGE,"E67")])]})]});
            fillet(context, id + "F14", {"entities" : qUnion([Q0, Q1, Q2, Q3, Q4, Q5]), "radius" : 3 * mm, "tangentPropagation" : true, "allowEdgeOverflow" : false});
        }
        {
            var Q0;
            Q0=makeQuery(id+"F1.opExtrude","CAP_EDGE",EDGE,{"disambiguationData":[OSD([sQuery(id+"F0.wireOp",EDGE,"E1.bottom")])],"isStart":false});
            fillet(context, id + "F15", {"entities" : qUnion([Q0]), "radius" : 2 * mm, "tangentPropagation" : true, "allowEdgeOverflow" : false});
        }
        {
            var Q0;
            {var subQ0=sQuery(id+"F0.wireOp",EDGE,"E21.filletArc");var subQ1=sQuery(id+"F0.wireOp",EDGE,"E7");var subQ2=sQuery(id+"F0.wireOp",EDGE,"E6");var subQ3=sQuery(id+"F0.wireOp",EDGE,"E5");var subQ4=sQuery(id+"F0.wireOp",EDGE,"E4");var subQ5=sQuery(id+"F0.wireOp",EDGE,"E22.filletArc");var subQ6=sQuery(id+"F0.wireOp",EDGE,"E1.bottom");var subQ7=sQuery(id+"F0.wireOp",EDGE,"E1.right");var subQ8=sQuery(id+"F0.wireOp",EDGE,"E1.top");var subQ9=sQuery(id+"F0.wireOp",EDGE,"E1.left");var subQ10=sQuery(id+"F0.wireOp",EDGE,"E23.filletArc");var subQ11=sQuery(id+"F0.wireOp",EDGE,"E24.filletArc");Q0=makeQuery(id+"F2.boolean.opBoolean","SPLIT",FACE,{"disambiguationData":[TD([makeQuery(id+"F1.opExtrude","SWEPT_FACE",FACE,{"disambiguationData":[OSD([subQ6])]})])],"derivedFrom":makeQuery(id+"F1.opExtrude","CAP_FACE",FACE,{"disambiguationData":[OSD([subQ6,subQ8,subQ9,subQ7,subQ4,subQ3,subQ2,subQ1,subQ0,subQ5,subQ10,subQ11])],"isStart":true})});}
            var sketch = newSketch(context, id + "F16", { "sketchPlane" : qUnion([Q0])});
            skLineSegment(sketch, "E79.0", {"start": v(80, -80) * mm, "end": v(80, 80) * mm});
            skArc(sketch, "E79.1", {"start": v(80, 80) * mm, "mid": v(77.07, 87.07) * mm, "end": v(70, 90) * mm});
            skLineSegment(sketch, "E79.2", {"start": v(-70, 90) * mm, "end": v(70, 90) * mm});
            skArc(sketch, "E79.3", {"start": v(-70, 90) * mm, "mid": v(-77.07, 87.07) * mm, "end": v(-80, 80) * mm});
            skLineSegment(sketch, "E79.4", {"start": v(-80, -80) * mm, "end": v(-80, 80) * mm});
            skArc(sketch, "E79.5", {"start": v(70, -90) * mm, "mid": v(77.07, -87.07) * mm, "end": v(80, -80) * mm});
            skLineSegment(sketch, "E79.6", {"start": v(-70, -90) * mm, "end": v(70, -90) * mm});
            skArc(sketch, "E79.7", {"start": v(-80, -80) * mm, "mid": v(-77.07, -87.07) * mm, "end": v(-70, -90) * mm});
            skArc(sketch, "E79.8", {"start": v(-56.15, -48.18) * mm, "mid": v(0, -67.5) * mm, "end": v(56.15, -48.18) * mm});
            skArc(sketch, "E79.9", {"start": v(56.15, -48.18) * mm, "mid": v(58.99, -44.68) * mm, "end": v(60, -40.3) * mm});
            skLineSegment(sketch, "E79.10", {"start": v(60, 40.3) * mm, "end": v(60, -40.3) * mm});
            skArc(sketch, "E79.11", {"start": v(56.15, 48.18) * mm, "mid": v(0, 67.5) * mm, "end": v(-56.15, 48.18) * mm});
            skLineSegment(sketch, "E79.12", {"start": v(-60, 40.3) * mm, "end": v(-60, -40.3) * mm});
            skArc(sketch, "E79.13", {"start": v(-56.15, 48.18) * mm, "mid": v(-58.99, 44.68) * mm, "end": v(-60, 40.3) * mm});
            skArc(sketch, "E79.14", {"start": v(-60, -40.3) * mm, "mid": v(-58.99, -44.68) * mm, "end": v(-56.15, -48.18) * mm});
            skArc(sketch, "E79.15", {"start": v(60, 40.3) * mm, "mid": v(58.99, 44.68) * mm, "end": v(56.15, 48.18) * mm});
            skCircle(sketch, "E79.16", {"center": v(60, 67.5) * mm, "radius": 4 * mm});
            skCircle(sketch, "E79.17", {"center": v(-60, 67.5) * mm, "radius": 4 * mm});
            skCircle(sketch, "E79.18", {"center": v(-60, -67.5) * mm, "radius": 4 * mm});
            skCircle(sketch, "E79.19", {"center": v(60, -67.5) * mm, "radius": 4 * mm});
            skLineSegment(sketch, "E80", {"start": v(0, 90) * mm, "end": v(0, 120) * mm, "construction": true});
            skCircle(sketch, "E81", {"center": v(0, 120) * mm, "radius": 6 * mm});
            skLineSegment(sketch, "E82", {"start": v(-33, 90) * mm, "end": v(-15, 108) * mm});
            skLineSegment(sketch, "E83", {"start": v(-15, 108) * mm, "end": v(-15, 120) * mm});
            skLineSegment(sketch, "E84", {"start": v(33, 90) * mm, "end": v(15, 108) * mm});
            skLineSegment(sketch, "E85", {"start": v(15, 108) * mm, "end": v(15, 120) * mm});
            skArc(sketch, "E86", {"start": v(15, 120) * mm, "mid": v(0, 135) * mm, "end": v(-15, 120) * mm});
            skLineSegment(sketch, "E87", {"start": v(-80, 0) * mm, "end": v(80, 0) * mm, "construction": true});
            skArc(sketch, "E88.MirrorCS", {"start": v(60, -40.3) * mm, "mid": v(58.99, -44.68) * mm, "end": v(56.15, -48.18) * mm});
            skLineSegment(sketch, "E89.MirrorCS", {"start": v(-15, -108) * mm, "end": v(-15, -120) * mm});
            skLineSegment(sketch, "E90.MirrorCS", {"start": v(15, -108) * mm, "end": v(15, -120) * mm});
            skArc(sketch, "E91.MirrorCS", {"start": v(-56.15, -48.18) * mm, "mid": v(-58.99, -44.68) * mm, "end": v(-60, -40.3) * mm});
            skLineSegment(sketch, "E92.MirrorCS", {"start": v(0, -90) * mm, "end": v(0, -120) * mm, "construction": true});
            skLineSegment(sketch, "E93.MirrorCS", {"start": v(-33, -90) * mm, "end": v(-15, -108) * mm});
            skLineSegment(sketch, "E94.MirrorCS", {"start": v(33, -90) * mm, "end": v(15, -108) * mm});
            skArc(sketch, "E95.MirrorCS", {"start": v(56.15, -48.18) * mm, "mid": v(0, -67.5) * mm, "end": v(-56.15, -48.18) * mm});
            skArc(sketch, "E96.MirrorCS", {"start": v(15, -120) * mm, "mid": v(0, -135) * mm, "end": v(-15, -120) * mm});
            skCircle(sketch, "E97.MirrorC", {"center": v(0, -120) * mm, "radius": 6 * mm});
            skArc(sketch, "E98.MirrorCS", {"start": v(80, -80) * mm, "mid": v(77.07, -87.07) * mm, "end": v(70, -90) * mm});
            skSolve(sketch);
        }
        {
            var Q0;
            Q0 = qSketchRegion(id + "F16", true);
            var Q1;
            Q1=makeQuery(id+"F2.opExtrude","CAP_FACE",FACE,{"disambiguationData":[OSD([sQuery(id+"F0.wireOp",EDGE,"E12"),sQuery(id+"F0.wireOp",EDGE,"E13"),sQuery(id+"F0.wireOp",EDGE,"E14"),sQuery(id+"F0.wireOp",EDGE,"E15"),sQuery(id+"F0.wireOp",EDGE,"E17.filletArc"),sQuery(id+"F0.wireOp",EDGE,"E18.filletArc"),sQuery(id+"F0.wireOp",EDGE,"E19.filletArc"),sQuery(id+"F0.wireOp",EDGE,"E20.filletArc"),sQuery(id+"F0.wireOp",EDGE,"E25.0"),sQuery(id+"F0.wireOp",EDGE,"E25.1"),sQuery(id+"F0.wireOp",EDGE,"E25.2"),sQuery(id+"F0.wireOp",EDGE,"E25.3"),sQuery(id+"F0.wireOp",EDGE,"E25.4"),sQuery(id+"F0.wireOp",EDGE,"E25.5"),sQuery(id+"F0.wireOp",EDGE,"E25.6"),sQuery(id+"F0.wireOp",EDGE,"E25.7")])],"isStart":false});
            extrude(context, id + "F17", {"entities" : qUnion([Q0]), "endBound" : BoundingType.UP_TO_SURFACE, "depth" : 25 * mm, "endBoundEntityFace" : qUnion([Q1]), "offsetDistance" : 25 * mm});
        }
    });
